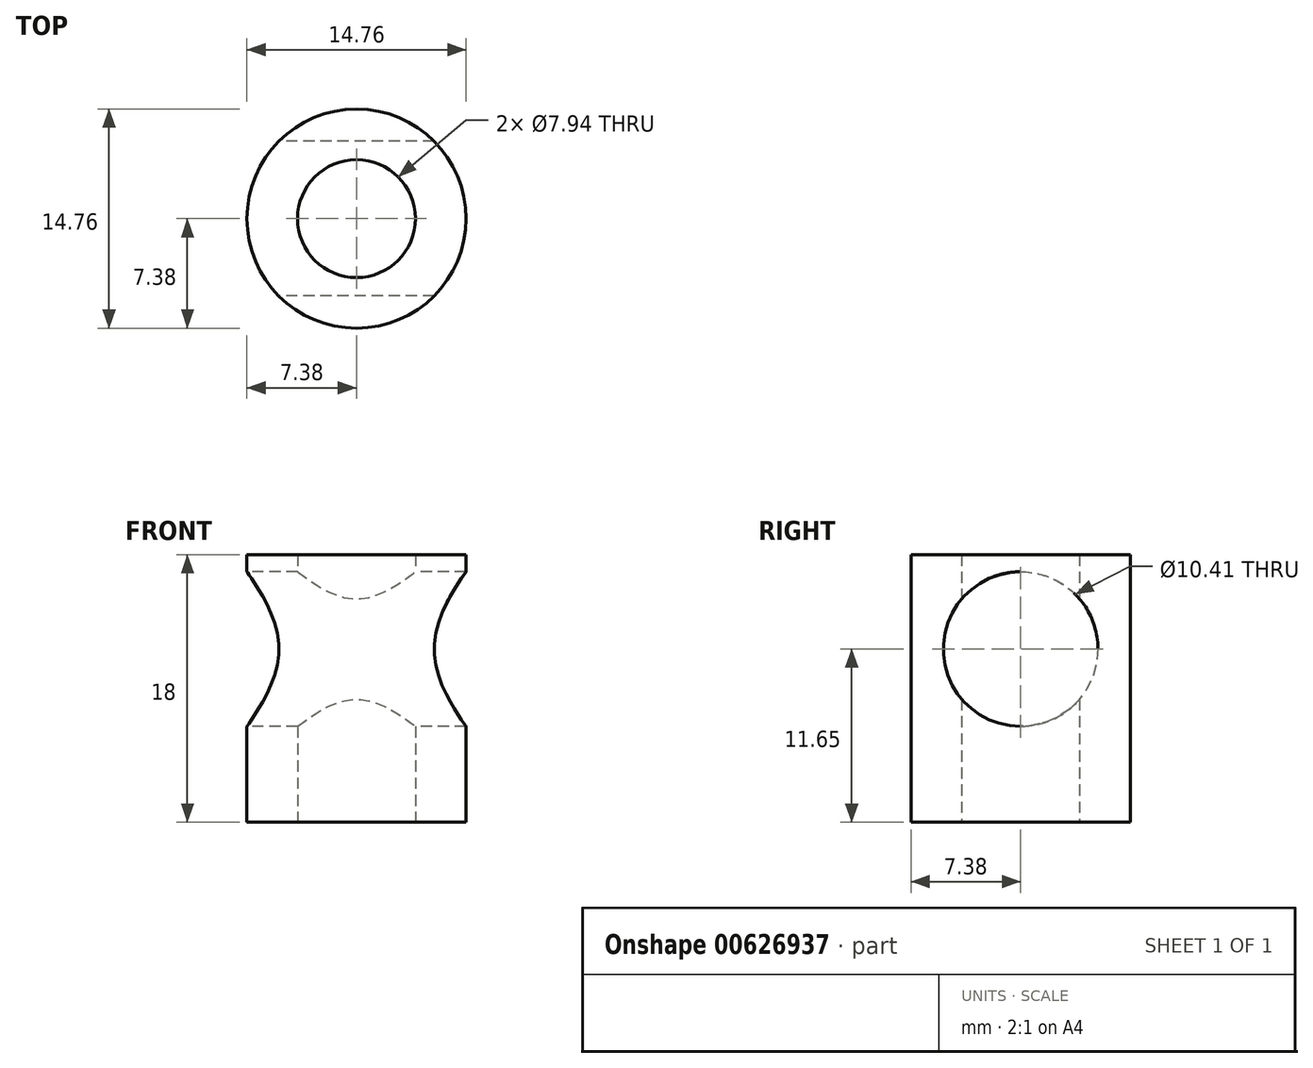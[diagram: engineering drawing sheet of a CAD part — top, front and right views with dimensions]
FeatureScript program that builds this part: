
annotation { "Feature Type Name" : "Feature", "Feature Type Description" : "" }
export const myFeature = defineFeature(function(context is Context, id is Id, definition is map)
    precondition{}
    {
        {
            var Q0;
            Q0=qCreatedBy(makeId("Top.planeOp"),FACE);
            var sketch = newSketch(context, id + "F0", { "sketchPlane" : qUnion([Q0])});
            skCircle(sketch, "E0", {"center": v(0, 0) * mm, "radius": 7.38 * mm});
            skSolve(sketch);
        }
        {
            var Q0;
            Q0=makeQuery(id+"F0.imprint","IMPRINT",FACE,{"disambiguationData":[TD([[makeQuery(id+"F0.imprint","IMPRINT",EDGE,{"derivedFrom":sQuery(id+"F0.wireOp",EDGE,"E0")}),1.0]])]});
            extrude(context, id + "F1", {"entities" : qUnion([Q0]), "depth" : 18 * mm, "offsetDistance" : 25.4 * mm});
        }
        {
            var Q0;
            Q0=makeQuery(id+"F1.opExtrude","CAP_FACE",FACE,{"disambiguationData":[OSD([sQuery(id+"F0.wireOp",EDGE,"E0")])],"isStart":false});
            var sketch = newSketch(context, id + "F2", { "sketchPlane" : qUnion([Q0])});
            skPoint(sketch, "E1", {"position": v(0, 0) * mm});
            skPoint(sketch, "E2", {"position": v(-7.38, 0) * mm});
            skSolve(sketch);
        }
        {
            var Q0;
            Q0=qCreatedBy(makeId("Right.planeOp"),FACE);
            var Q1;
            Q1=sQuery(id+"F2.wireOp",VERTEX,"E2");
            cPlane(context, id + "F3", {"entities" : qUnion([Q0, Q1]), "cplaneType" : CPlaneType.PLANE_POINT, "offset" : 25.4 * mm, "width" : 152.4 * mm, "height" : 152.4 * mm});
        }
        {
            var Q0;
            Q0=qCreatedBy(id+"F3.planeOp",FACE);
            var sketch = newSketch(context, id + "F4", { "sketchPlane" : qUnion([Q0])});
            skCircle(sketch, "E3", {"center": v(0, 11.65) * mm, "radius": 5.2 * mm});
            skSolve(sketch);
        }
        {
            var Q0;
            Q0=makeQuery(id+"F4.imprint","IMPRINT",FACE,{"disambiguationData":[TD([[makeQuery(id+"F4.imprint","IMPRINT",EDGE,{"derivedFrom":sQuery(id+"F4.wireOp",EDGE,"E3")}),1.0]])]});
            extrude(context, id + "F5", {"entities" : qUnion([Q0]), "operationType" : NewBodyOperationType.REMOVE, "endBound" : BoundingType.THROUGH_ALL, "depth" : 25.4 * mm, "offsetDistance" : 25.4 * mm});
        }
        {
            var Q0;
            Q0=sQuery(id+"F2.wireOp",VERTEX,"E1");
            var Q1;
            Q1=makeQuery(id+"F1.opExtrude","SWEPT_BODY",BODY,{"disambiguationData":[OSD([sQuery(id+"F0.wireOp",EDGE,"E0")])]});
            hole(context, id + "F6", {"style" : HoleStyle.SIMPLE, "endStyle" : HoleEndStyle.THROUGH, "standardTappedOrClearance" : lookupTablePath({ "standard" : "ANSI", "engagement" : "75%", "pitch" : "16 tpi", "size" : "3/8", "type" : "Tapped" }), "standardBlindInLast" : lookupTablePath({ "standard" : "ANSI", "engagement" : "75%", "pitch" : "16 tpi", "size" : "3/8", "type" : "Tapped" }), "holeDiameter" : 7.94 * mm, "majorDiameter" : 9.52 * mm, "showTappedDepth" : true, "isTappedThrough" : true, "tappedDepth" : 4.44 * mm, "tapClearance" : 3, "locations" : qUnion([Q0]), "scope" : qUnion([Q1]), "startStyle" : HoleStartStyle.PART});
        }
    });
